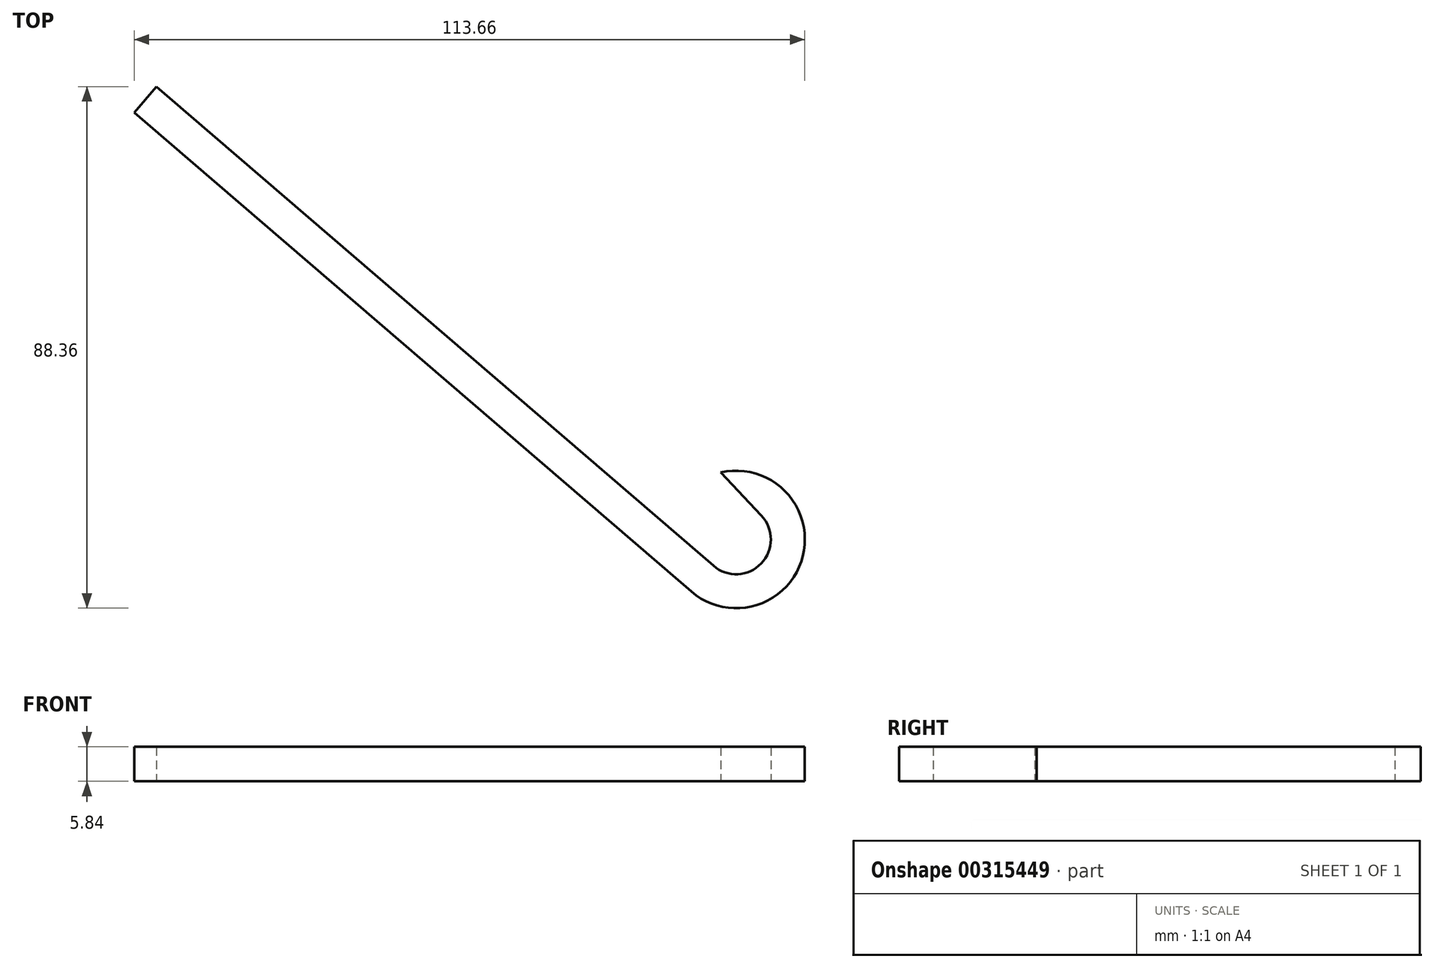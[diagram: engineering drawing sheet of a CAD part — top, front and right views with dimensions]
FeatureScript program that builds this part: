
annotation { "Feature Type Name" : "Feature", "Feature Type Description" : "" }
export const myFeature = defineFeature(function(context is Context, id is Id, definition is map)
    precondition{}
    {
        {
            var Q0;
            Q0=qCreatedBy(makeId("Top.planeOp"),FACE);
            var sketch = newSketch(context, id + "F0", { "sketchPlane" : qUnion([Q0])});
            skLineSegment(sketch, "E0", {"start": v(-54.38, 38.46) * mm, "end": v(40.04, -42.73) * mm});
            skLineSegment(sketch, "E1", {"start": v(43.8, -38.36) * mm, "end": v(-50.62, 42.82) * mm});
            skLineSegment(sketch, "E2", {"start": v(-54.38, 38.46) * mm, "end": v(-50.62, 42.82) * mm});
            skLineSegment(sketch, "E3", {"start": v(-50.62, 42.82) * mm, "end": v(-50.62, 42.82) * mm});
            skArc(sketch, "E4", {"start": v(40.04, -42.73) * mm, "mid": v(58.94, -36.69) * mm, "end": v(45.02, -22.55) * mm});
            skArc(sketch, "E5", {"start": v(43.8, -38.36) * mm, "mid": v(51.9, -37.96) * mm, "end": v(51.91, -29.86) * mm});
            skLineSegment(sketch, "E6", {"start": v(51.91, -29.86) * mm, "end": v(45.02, -22.55) * mm});
            skSolve(sketch);
        }
        {
            var Q0;
            Q0 = qSketchRegion(id + "F0", true);
            extrude(context, id + "F1", {"entities" : qUnion([Q0]), "depth" : 5.84 * mm});
        }
    });
